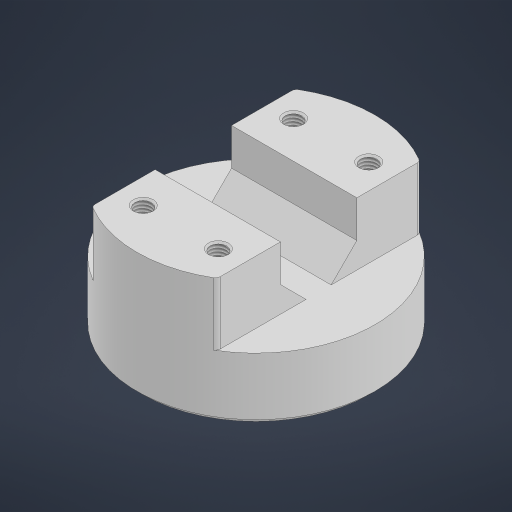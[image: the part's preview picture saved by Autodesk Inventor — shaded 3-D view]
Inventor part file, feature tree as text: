
AUTODESK INVENTOR PART (.ipt)
format: ipt  version: 2024.3 (Build 283343000, 343)  size: 463,360 bytes
history: native  units: mm
features: sketch x5, extrude x3, hole x1, fillet x1, chamfer x1, other x1, projected_geometry x1
ambient origin geometry x8: Origin, YZ Plane, XZ Plane, XY Plane, X Axis, Y Axis, Z Axis, Center Point
bodies: Solid1 (feature_tree)
feature tree (13):
  extrude  "Extrusion1"  Depth=50.0mm TaperAngle=0.0deg
  extrude  "Extrusion3"  TaperAngle=45.0deg  [1 undecoded]
  extrude  "Extrusion4"  Depth=25.0mm
  hole  "Hole2"  [1 undecoded]
  fillet  "Fillet1"  Radius=10.0mm
  chamfer  "Chamfer3"  Distance=60.0mm
  other  "Mark1"
  sketch  "Sketch1"  dims[d0=95.0mm d1=50.0mm d2=0.0mm]
  sketch  "Sketch4"  dims[d22=30.5mm d23=45.0deg]
  projected_geometry  "Projected Loop1"
  sketch  "Sketch5"  dims[d24=10.0mm d25=25.0mm]
  sketch  "Sketch6"  dims[d26=0.0mm d27=0.0mm d28=50.0mm d29=10.0mm d30=0.0mm]
  sketch  "Sketch7"  dims[d31=30.0mm d32=60.0mm d33=6.647mm d34=16.0mm d35=8.0mm d36=2.0mm d37=90.0deg d38=20.4mm d39=20.594885mm d40=2.0mm d41=2.0mm d42=2.0mm d43=45.0deg d44=4.0mm d45=30.0mm]
note: 2 required parameter values undecoded (feature->parameter linkage not recoverable at this tier; creation-order binding heuristic only, values carry confidence <= 0.55)
